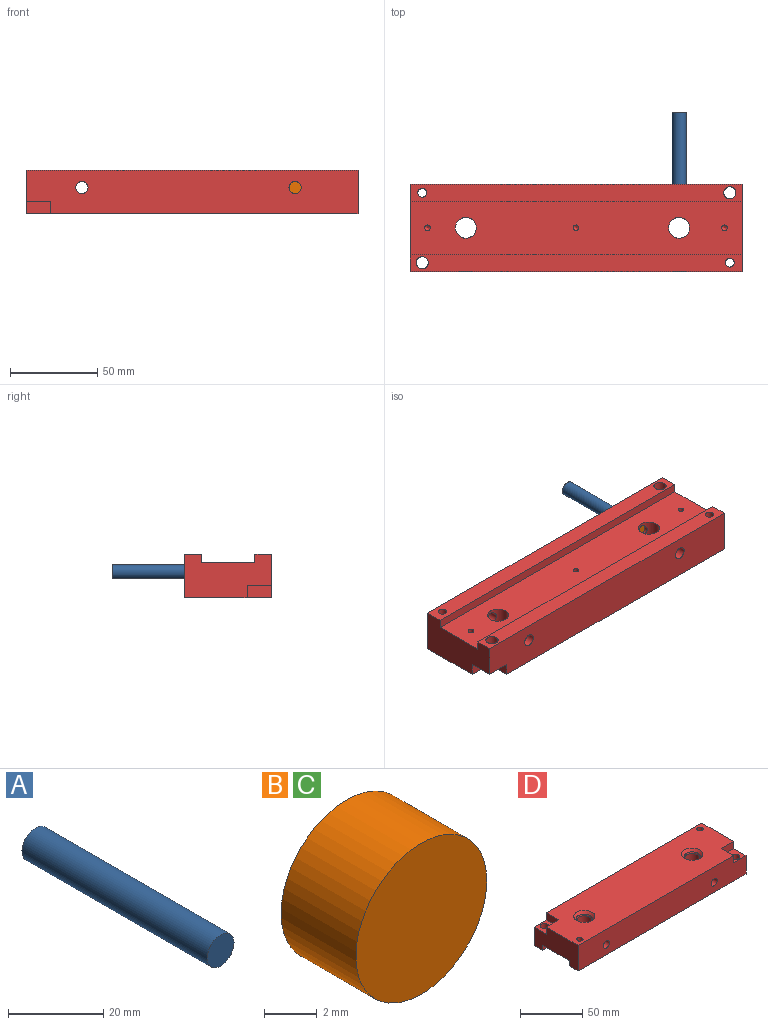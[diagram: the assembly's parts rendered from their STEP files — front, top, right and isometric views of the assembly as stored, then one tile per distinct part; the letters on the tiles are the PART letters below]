
ASSEMBLY  parts=4 mates=4
PART A: 3 faces, bbox 8x55x8 mm
  f0: cylinder r=4mm len=55mm, axis (0,1,0), area 1382.3mm2, adj f1,f2
  f1: plane 8x8mm, normal (0,-1,0), area 50.3mm2, adj f0
  f2: plane 8x8mm, normal (0,1,0), area 50.3mm2, adj f0
PART B: 3 faces, bbox 7x4x7 mm
  f0: cylinder r=3.5mm len=7mm, axis (0,1,0), area 88mm2, adj f1,f2
  f1: plane 7x7mm, normal (0,-1,0), area 38.5mm2, adj f0
  f2: plane 7x7mm, normal (0,1,0), area 38.5mm2, adj f0
PART C: same geometry as B
PART D: 36 faces, bbox 190x50x25 mm
  f0: cylinder r=6mm len=16.38mm, axis (0,0,1), area 536.9mm2, adj f22,f25,f34,f35
  f1: cylinder r=6mm len=16.38mm, axis (0,0,1), area 536.9mm2, adj f21,f25,f32,f33
  f2: plane 50x25mm, normal (-1,0,0), area 999.5mm2, adj f3,f5,f6,f7,f8,f10,f11,f23
  f3: plane 190x10mm, normal (0,0,-1), area 1841.9mm2, adj f2,f4,f5,f16,f17,f24
  f4: plane 50x25mm, normal (1,0,0), area 999.5mm2, adj f3,f5,f6,f7,f8,f13,f14,f23
  f5: plane 190x25mm, normal (0,-1,0), area 4575mm2, adj f2,f3,f4,f6,f12,f14,f32,f34
  f6: plane 190x50mm, normal (0,0,1), area 8614.8mm2, adj f2,f4,f5,f8,f9,f10,f12,f13
  f7: plane 190x9.5mm, normal (0,0,-1), area 1746.9mm2, adj f2,f4,f8,f15,f18,f23
  f8: plane 190x25mm, normal (0,1,0), area 4575mm2, adj f2,f4,f6,f7,f9,f11,f33,f35
  f9: plane 14x7mm, normal (-1,0,0), area 98mm2, adj f6,f8,f10,f11
  f10: plane 14x7mm, normal (0,1,0), area 98mm2, adj f2,f6,f9,f11
  f11: plane 14x14mm, normal (0,0,1), area 157.5mm2, adj f2,f8,f9,f10,f15
  f12: plane 14x7mm, normal (1,0,0), area 98mm2, adj f5,f6,f13,f14
  f13: plane 14x7mm, normal (0,-1,0), area 98mm2, adj f4,f6,f12,f14
  f14: plane 14x14mm, normal (0,0,1), area 157.5mm2, adj f4,f5,f12,f13,f16
  f15: cylinder r=3.5mm len=18mm, axis (0,0,1), area 395.8mm2, adj f7,f11
  f16: cylinder r=3.5mm len=18mm, axis (0,0,1), area 395.8mm2, adj f3,f14
  f17: cylinder r=2.5mm len=25mm, axis (0,0,1), area 392.7mm2, adj f3,f6
  f18: cylinder r=2.5mm len=25mm, axis (0,0,1), area 392.7mm2, adj f6,f7
  f19: cone r=6mm half-angle=41deg, axis (0,0,1), area 144.2mm2, adj f6,f21
  f20: cone r=6mm half-angle=41deg, axis (0,0,1), area 144.2mm2, adj f6,f22
  f21: torus R=8mm, axis (0,0,-1), area 55.4mm2, adj f1,f19
  f22: torus R=8mm, axis (0,0,-1), area 55.4mm2, adj f0,f20
  f23: plane 190x5mm, normal (0,-1,0), area 950mm2, adj f2,f4,f7,f25
  f24: plane 190x5mm, normal (0,1,0), area 950mm2, adj f2,f3,f4,f25
  f25: plane 190x30.5mm, normal (0,0,-1), area 5544.7mm2, adj f0,f1,f2,f4,f23,f24,f26,f28
  f26: cylinder r=1.6mm len=14.25mm, axis (0,0,-1), area 143.3mm2, adj f25,f27
  f27: cone r=0mm half-angle=59deg, axis (0,0,-1), area 9.4mm2, adj f26
  f28: cylinder r=1.6mm len=14.25mm, axis (0,0,-1), area 143.3mm2, adj f25,f29
  f29: cone r=0mm half-angle=59deg, axis (0,0,-1), area 9.4mm2, adj f28
  f30: cylinder r=1.6mm len=14.25mm, axis (0,0,-1), area 143.3mm2, adj f25,f31
  f31: cone r=0mm half-angle=59deg, axis (0,0,-1), area 9.4mm2, adj f30
  f32: cylinder r=3.5mm len=20.13mm, axis (0,-1,0), area 429.9mm2, adj f1,f5
  f33: cylinder r=3.5mm len=20.13mm, axis (0,-1,0), area 429.9mm2, adj f1,f8
  f34: cylinder r=3.5mm len=20.13mm, axis (0,-1,0), area 429.9mm2, adj f0,f5
  f35: cylinder r=3.5mm len=20.13mm, axis (0,-1,0), area 429.9mm2, adj f0,f8
PLACE A t=(-36,-70,10)mm
PLACE B t=(-36,-125,10)mm
PLACE C t=(-36,-113,10)mm
PLACE D rot(axis=(1,0,0),180deg) t=(0,-161,20)mm
MATE fastened B.f0 <-> A.f0  axis (0,1,0) through (-36,-125,10)mm
MATE fastened D.f34 <-> A.f0  axis (0,-1,0) through (-36,-161,10)mm
MATE fastened C.f0 <-> A.f0  axis (0,1,0) through (-36,-113,10)mm
MATE fastened C.f0 <-> A.f0  axis (0,-1,0) through (-36,-117,10)mm
